# Revit family: Drain_Kettle_Zurn-Z1762
name_source: partatom
category: Plumbing Fixtures
units: mm (PartAtom-declared; Revit-internal decimal feet)

## family parameters
Always vertical = Yes
Cut with Voids When Loaded = No
Maintain Annotation Orientation = No
OmniClass Number = 23.45.55.21
OmniClass Title = Drains (Wastes)
Part Type = Normal
Room Calculation Point = No
Round Connector Dimension = Use Radius
Shared = No
Work Plane-Based = No

## types (6) — shared parameters
Approx. Wt. Lbs = 71 "
Assembly Code = D2030300
CW Connection = No
Default Elevation = 25 "
Description = KETTLE DRAIN
Grate Open Area = 149 "
HW Connection = No
Manufacturer = Zurn Water, LLC
Manufacturer Brand = Zurn
Model = Z1762
Modified Date = 11/07/2025
Product Documentation Link = https://files.zurn.com
Product Page URL = https://www.zurn.com
Product data URL = https://www.bimobject.com
URL = www.zurn.com
Vent Connection = No
WFU = 1
Waste Connection = Yes
zero-valued in all types: CWFU, HWFU

## per-type parameters (varying)
| type | Main Material | Pipe Size A (Actual Radius) | Pipe Size A (Diameter) | Pipe Size A (Inner Radius) | Pipe Size A (Nominal Radius) | R Dimension |
| Z1762-3 Inch No-Hub Outlet | Steel - Zurn - Stainless - A.R.E Coated - Type - 304 | 1.75 " | 3 " | 1.534 " | 1.5 " | 7.875 " |
| Z1762-4 Inch No-Hub Outlet | Steel - Zurn - Stainless - A.R.E Coated - Type - 304 | 2.25 " | 4 " | 2.013 " | 2 " | 7.875 " |
| Z1762-6 Inch No-Hub Outlet | Steel - Zurn - Stainless - A.R.E Coated - Type - 304 | 3.313 " | 6 " | 3.033 " | 3 " | 6.875 " |
| ZS1762-3 Inch No-Hub Outlet | Steel - Zurn - Fabricated Stainless - Type - 304 | 1.75 " | 3 " | 1.534 " | 1.5 " | 7.875 " |
| ZS1762-4 Inch No-Hub Outlet | Steel - Zurn - Fabricated Stainless - Type - 304 | 2.25 " | 4 " | 2.013 " | 2 " | 7.875 " |
| ZS1762-6 Inch No-Hub Outlet | Steel - Zurn - Fabricated Stainless - Type - 304 | 3.313 " | 6 " | 3.033 " | 3 " | 6.875 " |

## geometry (parser evidence)
native form markers: Blend x4, Sweep x5
no freeform markers — native parametric forms only
